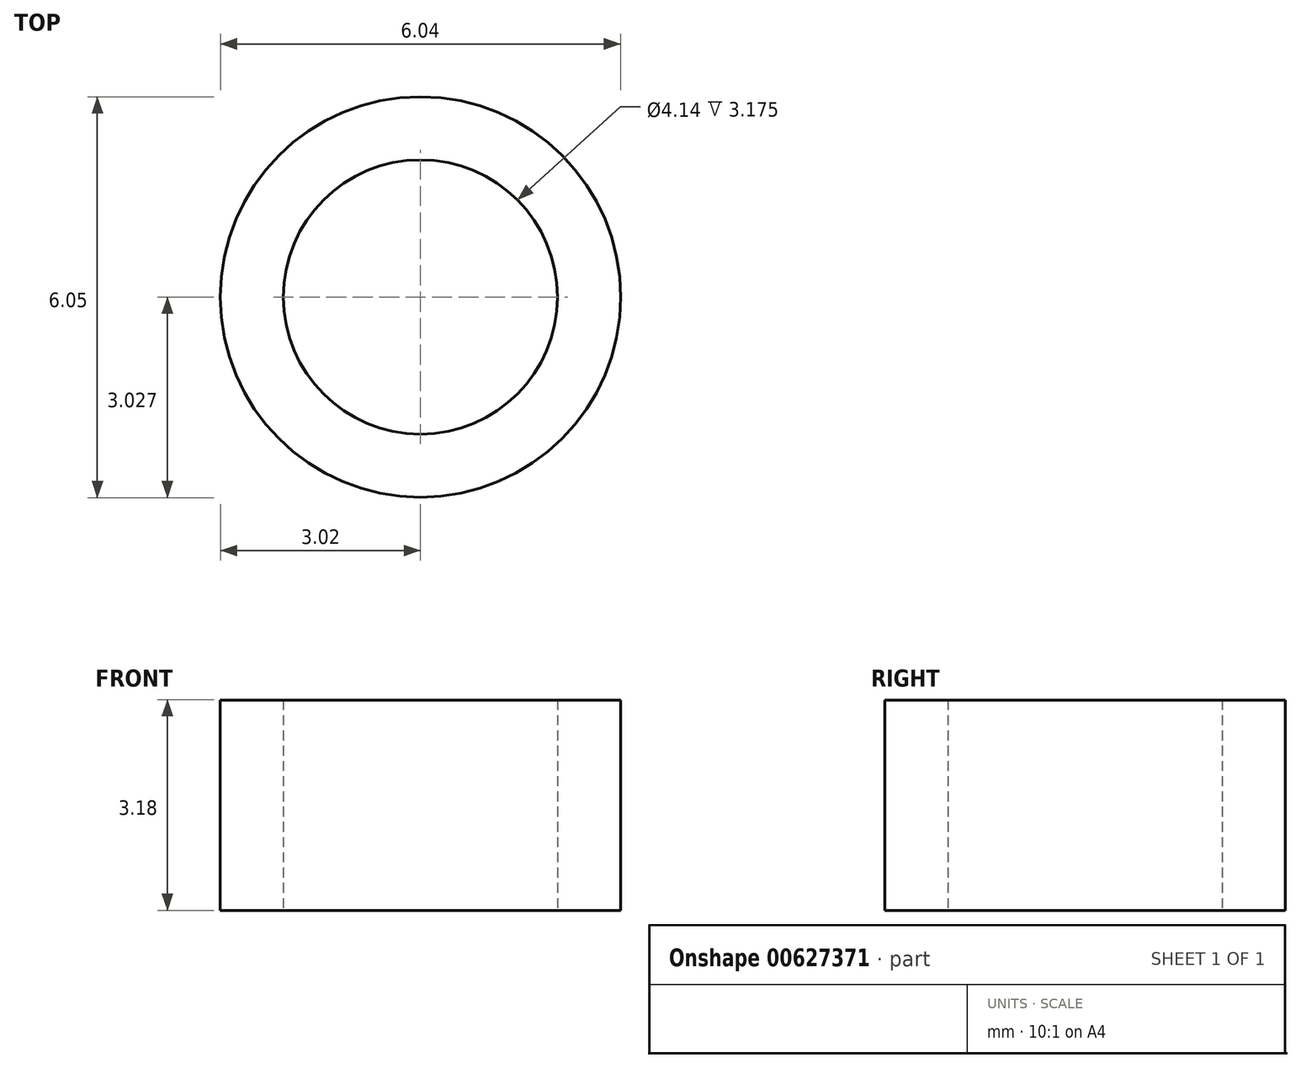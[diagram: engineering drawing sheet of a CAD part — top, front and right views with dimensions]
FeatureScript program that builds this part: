
annotation { "Feature Type Name" : "Feature", "Feature Type Description" : "" }
export const myFeature = defineFeature(function(context is Context, id is Id, definition is map)
    precondition{}
    {
        {
            var Q0;
            Q0=qCreatedBy(makeId("Top.planeOp"),FACE);
            var sketch = newSketch(context, id + "F0", { "sketchPlane" : qUnion([Q0])});
            skCircle(sketch, "E0", {"center": v(-50.03, -18.66) * mm, "radius": 3.02 * mm});
            skCircle(sketch, "E1", {"center": v(-50.03, -18.66) * mm, "radius": 2.07 * mm});
            skSolve(sketch);
        }
        {
            var Q0;
            Q0=makeQuery(id+"F0.imprint","IMPRINT",FACE,{"disambiguationData":[TD([[makeQuery(id+"F0.imprint","IMPRINT",EDGE,{"derivedFrom":sQuery(id+"F0.wireOp",EDGE,"E0")}),1.0]])]});
            extrude(context, id + "F1", {"entities" : qUnion([Q0]), "depth" : 3.17 * mm, "offsetDistance" : 25.4 * mm});
        }
    });
